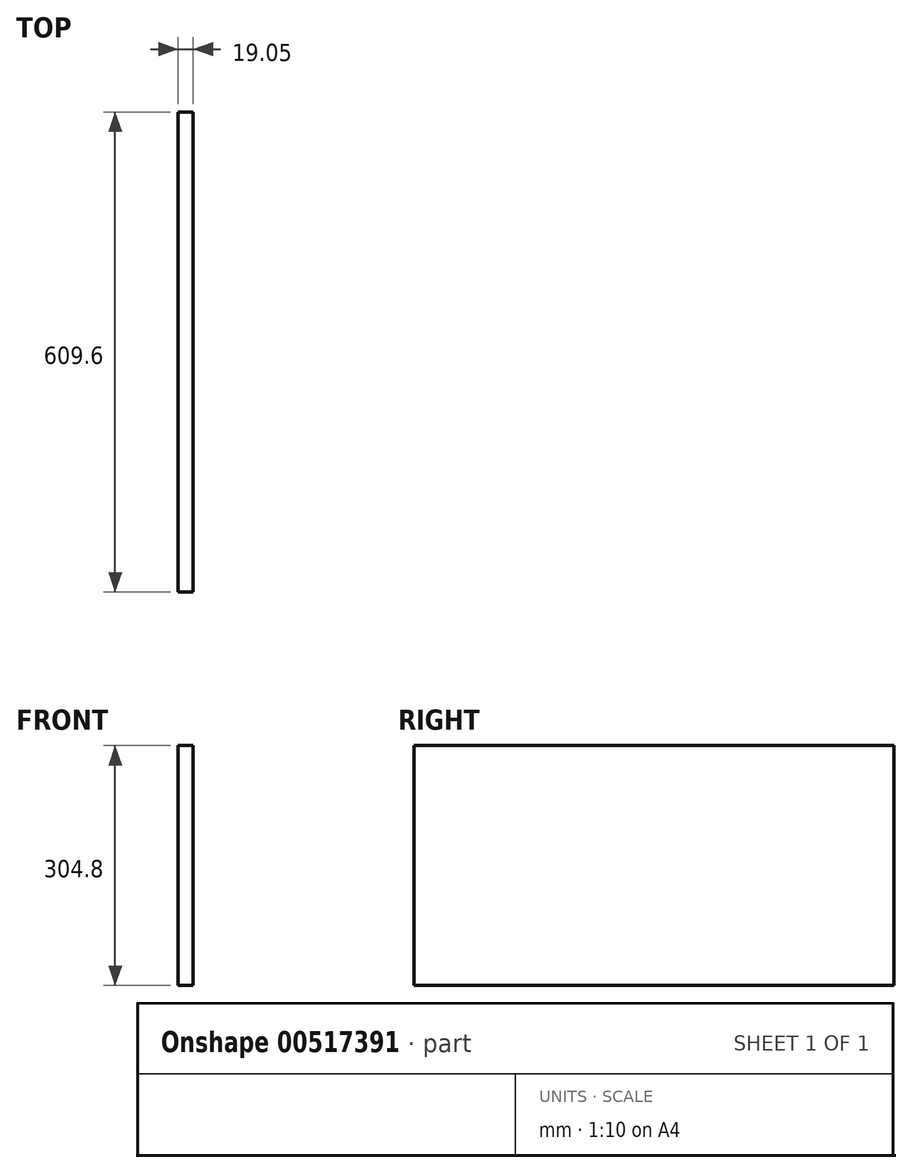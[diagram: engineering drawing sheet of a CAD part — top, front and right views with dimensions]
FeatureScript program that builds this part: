
annotation { "Feature Type Name" : "Feature", "Feature Type Description" : "" }
export const myFeature = defineFeature(function(context is Context, id is Id, definition is map)
    precondition{}
    {
        {
            var Q0;
            Q0=qCreatedBy(makeId("Right.planeOp"),FACE);
            var sketch = newSketch(context, id + "F0", { "sketchPlane" : qUnion([Q0])});
            skLineSegment(sketch, "E0.bottom", {"start": v(-304.8, 152.4) * mm, "end": v(304.8, 152.4) * mm});
            skLineSegment(sketch, "E0.top", {"start": v(-304.8, -152.4) * mm, "end": v(304.8, -152.4) * mm});
            skLineSegment(sketch, "E0.left", {"start": v(-304.8, 152.4) * mm, "end": v(-304.8, -152.4) * mm});
            skLineSegment(sketch, "E0.right", {"start": v(304.8, 152.4) * mm, "end": v(304.8, -152.4) * mm});
            skPoint(sketch, "E0.middle", {"position": v(0, 0) * mm});
            skSolve(sketch);
        }
        {
            var Q0;
            Q0 = qSketchRegion(id + "F0", true);
            extrude(context, id + "F1", {"entities" : qUnion([Q0]), "depth" : 19.05 * mm});
        }
    });
